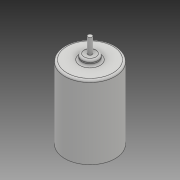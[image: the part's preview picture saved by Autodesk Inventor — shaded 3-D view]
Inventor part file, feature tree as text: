
AUTODESK INVENTOR PART (.ipt)
format: ipt  version: 2018 (Build 220112000, 112)  size: 109,568 bytes
history: native  units: mm
features: extrude x3, sketch x3, other x1, fillet x1
ambient origin geometry x8: Origin, YZ Plane, XZ Plane, XY Plane, X Axis, Y Axis, Z Axis, Center Point
bodies: Body1 (feature_tree)
feature tree (8):
  other  "ソリッド1"
  extrude  "押し出し1"  Depth=36.0mm
  extrude  "押し出し2"  Depth=52.5mm TaperAngle=0.0deg
  extrude  "押し出し3"  Depth=11.5mm
  fillet  "フィレット1"  Radius=3.8mm
  sketch  "スケッチ1"
  sketch  "スケッチ2"
  sketch  "スケッチ3"
